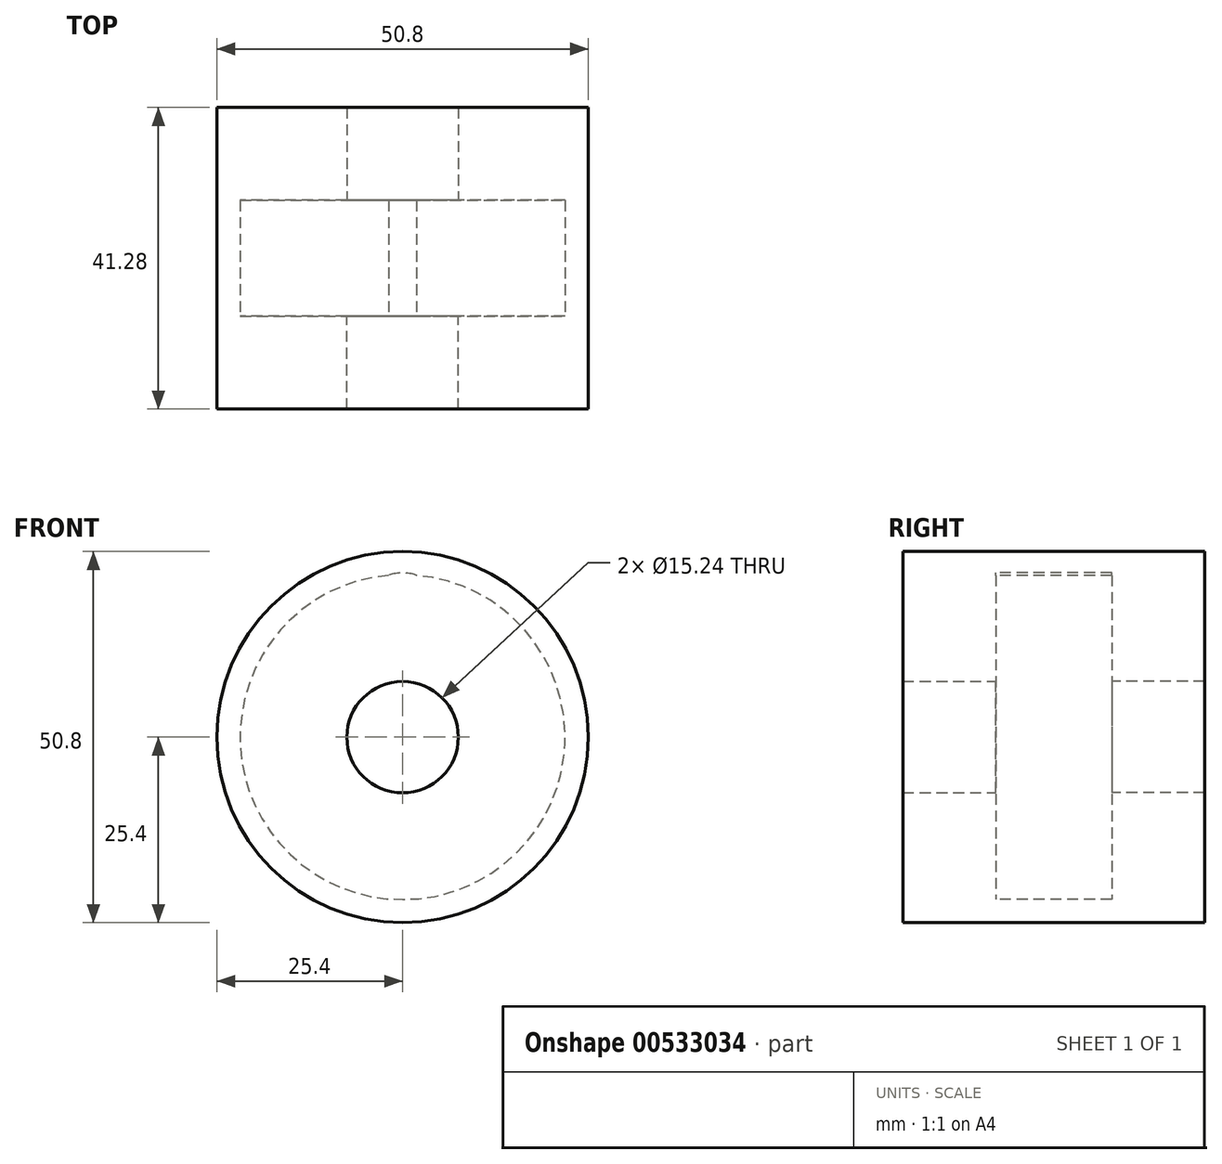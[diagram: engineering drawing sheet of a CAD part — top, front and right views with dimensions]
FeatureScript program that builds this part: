
annotation { "Feature Type Name" : "Feature", "Feature Type Description" : "" }
export const myFeature = defineFeature(function(context is Context, id is Id, definition is map)
    precondition{}
    {
        {
            var Q0;
            Q0=qCreatedBy(makeId("Front.planeOp"),FACE);
            var sketch = newSketch(context, id + "F0", { "sketchPlane" : qUnion([Q0])});
            skCircle(sketch, "E0", {"center": v(0, 0) * mm, "radius": 7.62 * mm});
            skCircle(sketch, "E1", {"center": v(0, 0) * mm, "radius": 25.4 * mm});
            skSolve(sketch);
        }
        {
            var Q0;
            Q0=makeQuery(id+"F0.imprint","IMPRINT",FACE,{"disambiguationData":[TD([[makeQuery(id+"F0.imprint","IMPRINT",EDGE,{"derivedFrom":sQuery(id+"F0.wireOp",EDGE,"E0")}),-1.0]])]});
            extrude(context, id + "F1", {"entities" : qUnion([Q0]), "depth" : 12.7 * mm, "offsetDistance" : 25.4 * mm});
        }
        {
            var Q0;
            Q0=makeQuery(id+"F1.opExtrude","CAP_FACE",FACE,{"disambiguationData":[OSD([sQuery(id+"F0.wireOp",EDGE,"E0"),sQuery(id+"F0.wireOp",EDGE,"E1")])],"isStart":true});
            var sketch = newSketch(context, id + "F2", { "sketchPlane" : qUnion([Q0])});
            skArc(sketch, "E2", {"start": v(-1.9, 22.14) * mm, "mid": v(0, -22.23) * mm, "end": v(1.9, 22.14) * mm});
            skCircle(sketch, "E3", {"center": v(0, 0) * mm, "radius": 25.4 * mm});
            skLineSegment(sketch, "E4", {"start": v(29.32, 22.23) * mm, "end": v(1.67, 22.23) * mm, "construction": true});
            skLineSegment(sketch, "E5", {"start": v(0, 0) * mm, "end": v(0, 17.1) * mm, "construction": true});
            skLineSegment(sketch, "E6", {"start": v(16.14, 22.48) * mm, "end": v(-17.78, 22.48) * mm, "construction": true});
            skLineSegment(sketch, "E7", {"start": v(1.9, 20.88) * mm, "end": v(1.9, 16.62) * mm, "construction": true});
            skLineSegment(sketch, "E8", {"start": v(-1.9, 21.04) * mm, "end": v(-1.9, 16.05) * mm, "construction": true});
            skArc(sketch, "E9", {"start": v(1.9, 22.14) * mm, "mid": v(0, 22.5) * mm, "end": v(-1.9, 22.14) * mm});
            skLineSegment(sketch, "E10.trimOffspring", {"start": v(-1.67, 22.23) * mm, "end": v(-38.22, 22.22) * mm, "construction": true});
            skLineSegment(sketch, "E11.trimOffspring", {"start": v(0, 22.5) * mm, "end": v(0, 39.34) * mm, "construction": true});
            skSolve(sketch);
        }
        {
            var Q0;
            Q0 = qSketchRegion(id + "F2", true);
            extrude(context, id + "F3", {"entities" : qUnion([Q0]), "operationType" : NewBodyOperationType.ADD, "depth" : 15.88 * mm, "offsetDistance" : 25.4 * mm});
        }
        {
            var Q0;
            Q0=makeQuery(id+"F3.opExtrude","CAP_FACE",FACE,{"disambiguationData":[OSD([sQuery(id+"F2.wireOp",EDGE,"E2"),sQuery(id+"F2.wireOp",EDGE,"E3"),sQuery(id+"F2.wireOp",EDGE,"E9")])],"isStart":false});
            var sketch = newSketch(context, id + "F4", { "sketchPlane" : qUnion([Q0])});
            skCircle(sketch, "E12", {"center": v(0, 0) * mm, "radius": 7.62 * mm});
            skCircle(sketch, "E13", {"center": v(0, 0) * mm, "radius": 25.4 * mm});
            skSolve(sketch);
        }
        {
            var Q0;
            Q0 = qSketchRegion(id + "F4", true);
            extrude(context, id + "F5", {"entities" : qUnion([Q0]), "operationType" : NewBodyOperationType.ADD, "depth" : 12.7 * mm, "offsetDistance" : 25.4 * mm});
        }
    });
